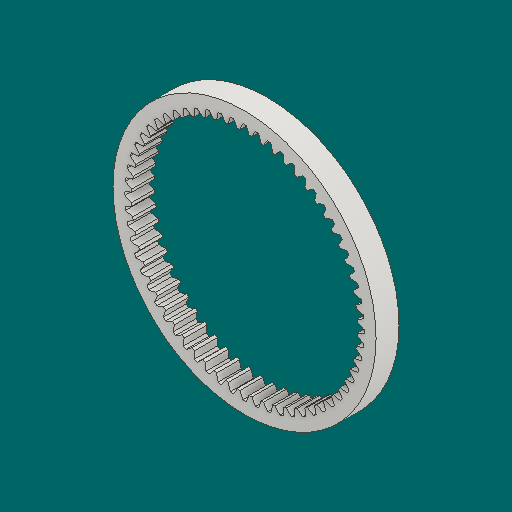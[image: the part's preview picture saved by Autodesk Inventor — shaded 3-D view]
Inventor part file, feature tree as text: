
AUTODESK INVENTOR PART (.ipt)
format: ipt  version: 2023.1 (Build 271208000, 208)  size: 369,152 bytes
history: native  units: mm (DEFAULTED — no unit token found)
features: plane x3, other x3, sketch x2, extrude x1
ambient origin geometry x8: Origin, YZ Plane, XZ Plane, XY Plane, X Axis, Y Axis, Z Axis, Center Point
bodies: Solid1 (feature_tree)
feature tree (9):
  extrude  "Extrusion1"  Depth=7.62mm TaperAngle=0.0deg
  plane  "Work Plane1"
  plane  "Work Plane2"
  plane  "Work Plane3"
  other  "Spur Gear"
  sketch  "Sketch1"  dims[d0=87.3125mm d1=7.62mm d2=0.0mm]
  sketch  "Sketch2"  dims[d3=76.2mm d4=76.2mm d5=0.0mm d6=0.0mm d7=0.523599mm d9=0.0mm d14=0.0mm d15=26.67mm d16=0.0mm d17=0.0mm d18=0.0mm d19=26.67mm]
  other  "Srf1"
  other  "Pitch Diameter"
